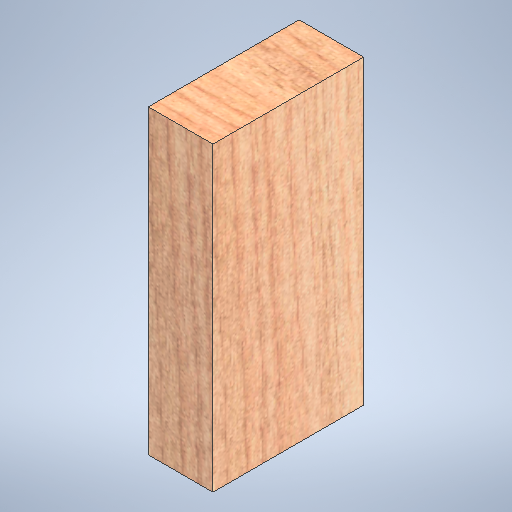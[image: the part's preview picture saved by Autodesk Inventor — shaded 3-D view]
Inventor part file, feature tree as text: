
AUTODESK INVENTOR PART (.ipt)
format: ipt  version: 2025.1 (Build 291241020, 241B)  size: 445,952 bytes
history: native  units: in
note: dims shown in document units (in); Inventor stores cm internally (conversion verified against a paired STEP export)
features: extrude x1, sketch x1
ambient origin geometry x8: Origin, YZ Plane, XZ Plane, XY Plane, X Axis, Y Axis, Z Axis, Center Point
bodies: Solid1 (feature_tree)
feature tree (2):
  extrude  "Extrusion1"  Depth=1.5in
  sketch  "Sketch1"  dims[d0=3.5in d1=1.5in d2=7.0in d3=0.0in]
